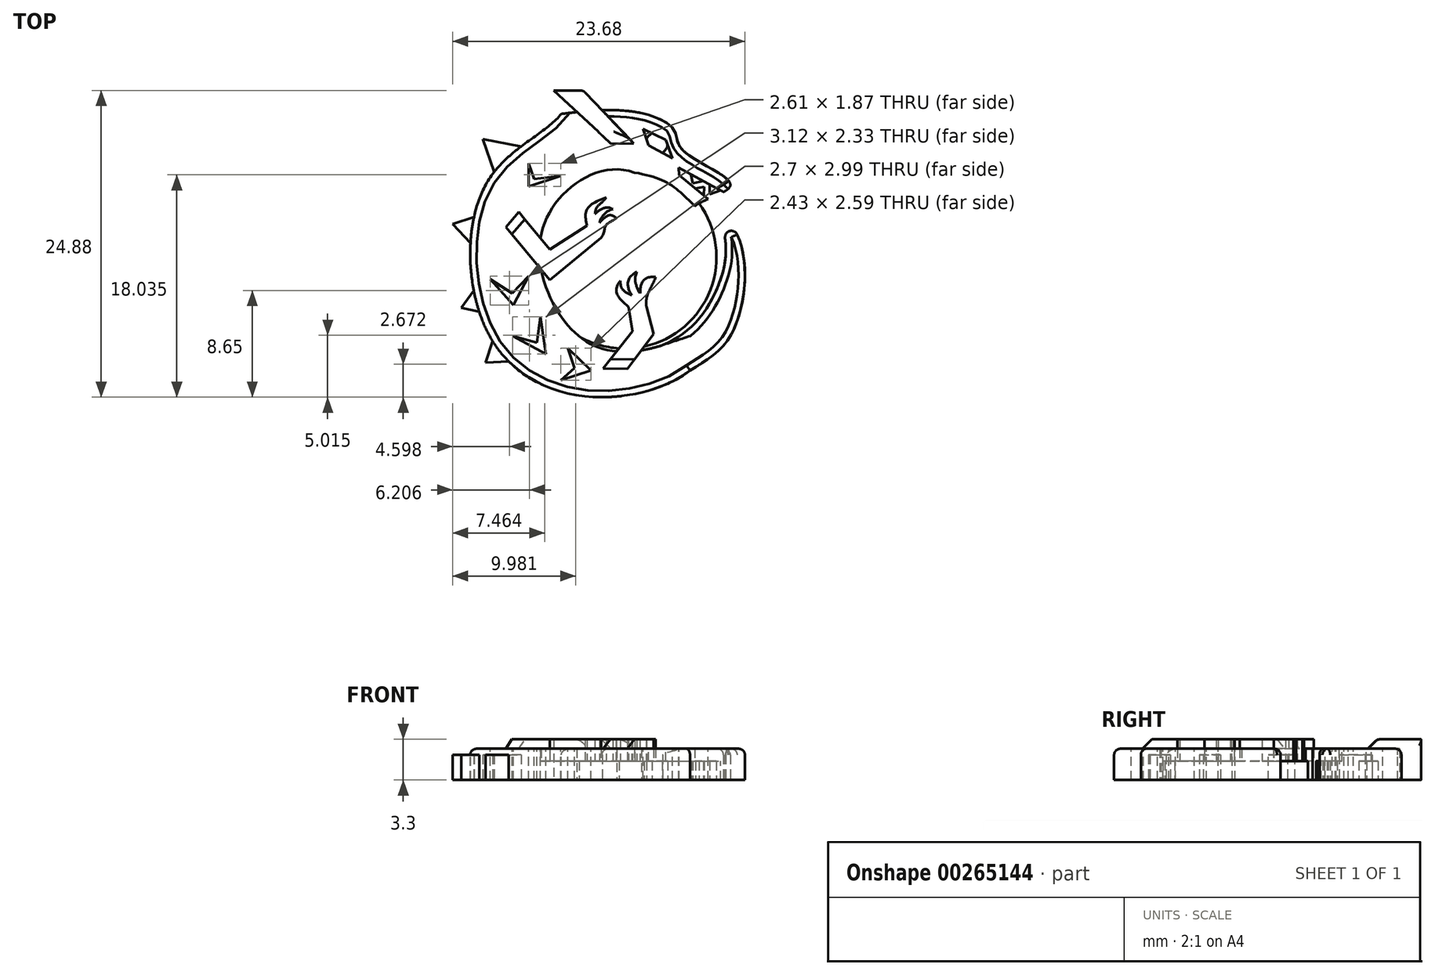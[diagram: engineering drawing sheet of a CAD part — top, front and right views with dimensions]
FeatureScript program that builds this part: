
annotation { "Feature Type Name" : "Feature", "Feature Type Description" : "" }
export const myFeature = defineFeature(function(context is Context, id is Id, definition is map)
    precondition{}
    {
        {
            var Q0;
            Q0=qCreatedBy(makeId("Top.planeOp"),FACE);
            var sketch = newSketch(context, id + "F0", { "sketchPlane" : qUnion([Q0])});
            skCircle(sketch, "E0", {"center": v(0, 0) * mm, "radius": 12.7 * mm, "construction": true});
            skCircle(sketch, "E1", {"center": v(0, 0) * mm, "radius": 7.43 * mm});
            skSolve(sketch);
        }
        {
            var Q0;
            Q0=makeQuery(id+"F0.imprint","IMPRINT",FACE,{"disambiguationData":[TD([[makeQuery(id+"F0.imprint","IMPRINT",EDGE,{"derivedFrom":sQuery(id+"F0.wireOp",EDGE,"E1")}),1.0]])]});
            var Q1;
            Q1=sQuery(id+"F0.wireOp",EDGE,"E1");
            extrude(context, id + "F1", {"entities" : qUnion([Q0]), "surfaceEntities" : qUnion([Q1]), "depth" : 1.52 * mm});
        }
        {
            var Q0;
            Q0=qCreatedBy(makeId("Top.planeOp"),FACE);
            var sketch = newSketch(context, id + "F2", { "sketchPlane" : qUnion([Q0])});
            skCircle(sketch, "E2", {"center": v(0, 0) * mm, "radius": 12.7 * mm, "construction": true});
            skFitSpline(sketch, "E3", {"points": [v(-5.15, 11.6) * mm, v(-11.13, 6.12) * mm, v(-10.71, -6.82) * mm, v(-2.1, -11.36) * mm, v(5.28, -9.2) * mm], "startDerivative": vector(-16.37, -21.23) * mm, "endDerivative": vector(20.97, 16.77) * mm});
            skFitSpline(sketch, "E4", {"points": [v(0.8, 6.85) * mm, v(-6.42, 2.98) * mm, v(-5.45, -4.38) * mm, v(-1.56, -7.5) * mm, v(3.08, -7.14) * mm], "startDerivative": vector(-30.12, 10.9) * mm, "endDerivative": vector(18.36, 6.12) * mm});
            skFitSpline(sketch, "E5", {"points": [v(3.08, -7.14) * mm, v(7.52, -2.43) * mm, v(7.7, 3.63) * mm], "startDerivative": vector(15.11, 6.36) * mm, "endDerivative": vector(-4.84, 17.51) * mm});
            skFitSpline(sketch, "E6", {"points": [v(5.28, -9.2) * mm, v(8.88, -5.74) * mm, v(9.73, -1.63) * mm, v(7.7, 3.63) * mm], "startDerivative": vector(21.68, 12.67) * mm, "endDerivative": vector(-13.83, 11.17) * mm});
            skFitSpline(sketch, "E7", {"points": [v(-5.15, 11.6) * mm, v(1.6, 11.6) * mm, v(3.97, 10.34) * mm, v(4.4, 9.04) * mm, v(6.87, 7.25) * mm, v(8.54, 5.76) * mm, v(5.68, 4.14) * mm], "startDerivative": vector(39.1, 4.84) * mm, "endDerivative": vector(-16.82, -11.68) * mm});
            skFitSpline(sketch, "E8", {"points": [v(0.8, 6.85) * mm, v(3.88, 5.76) * mm, v(5.68, 4.14) * mm], "startDerivative": vector(7.86, -1.41) * mm, "endDerivative": vector(3.87, -3.38) * mm});
            skSolve(sketch);
        }
        {
            var Q0;
            Q0 = qSketchRegion(id + "F2", true);
            extrude(context, id + "F3", {"entities" : qUnion([Q0]), "operationType" : NewBodyOperationType.ADD, "depth" : 2.54 * mm});
        }
        {
            var Q0;
            Q0=qCreatedBy(makeId("Top.planeOp"),FACE);
            var sketch = newSketch(context, id + "F4", { "sketchPlane" : qUnion([Q0])});
            skLineSegment(sketch, "E9", {"start": v(-1.93, 9.95) * mm, "end": v(-5.76, 13.5) * mm});
            skLineSegment(sketch, "E10", {"start": v(-5.76, 13.5) * mm, "end": v(-3.37, 13.5) * mm});
            skLineSegment(sketch, "E11", {"start": v(-3.37, 13.5) * mm, "end": v(0, 9.97) * mm});
            skLineSegment(sketch, "E12", {"start": v(0, 9.97) * mm, "end": v(-1.93, 9.95) * mm});
            skLineSegment(sketch, "E13", {"start": v(-8.1, 3.06) * mm, "end": v(-6.08, 0.61) * mm});
            skLineSegment(sketch, "E14", {"start": v(-6.08, 0.61) * mm, "end": v(-3.06, 2.54) * mm});
            skLineSegment(sketch, "E15", {"start": v(-8.1, 3.06) * mm, "end": v(-9.14, 1.84) * mm});
            skPoint(sketch, "E15.endSnap0", {"position": v(-7.09, 1.84) * mm});
            skLineSegment(sketch, "E16", {"start": v(-9.14, 1.84) * mm, "end": v(-6.08, -1.86) * mm});
            skLineSegment(sketch, "E17", {"start": v(-6.08, -1.86) * mm, "end": v(-1.93, 1.58) * mm});
            skLineSegment(sketch, "E18", {"start": v(-1.17, -8.27) * mm, "end": v(0.63, -6.04) * mm});
            skLineSegment(sketch, "E19", {"start": v(0.63, -6.04) * mm, "end": v(0.32, -4.04) * mm});
            skLineSegment(sketch, "E20", {"start": v(1.76, -4.04) * mm, "end": v(2.33, -6.23) * mm});
            skLineSegment(sketch, "E21", {"start": v(2.33, -6.23) * mm, "end": v(0.78, -8.3) * mm});
            skLineSegment(sketch, "E22", {"start": v(0.78, -8.3) * mm, "end": v(-1.17, -8.27) * mm});
            skFitSpline(sketch, "E23", {"points": [v(-3.06, 2.54) * mm, v(-3.06, 3.89) * mm, v(-1.5, 4.83) * mm], "startDerivative": vector(-0.67, 3.2) * mm, "endDerivative": vector(3.68, 1.43) * mm});
            skFitSpline(sketch, "E24", {"points": [v(-2.42, 3.49) * mm, v(-2.23, 4.07) * mm, v(-1.5, 4.83) * mm], "startDerivative": vector(0.18, 1.81) * mm, "endDerivative": vector(1.3, 1.74) * mm});
            skFitSpline(sketch, "E25", {"points": [v(0.32, -4.04) * mm, v(-0.6, -3.02) * mm, v(-0.36, -1.94) * mm], "startDerivative": vector(-2.36, 1.84) * mm, "endDerivative": vector(2.3, 2.4) * mm});
            skFitSpline(sketch, "E26", {"points": [v(-0.36, -1.94) * mm, v(-0.13, -2.69) * mm, v(0.57, -3.1) * mm], "startDerivative": vector(0.12, -2.92) * mm, "endDerivative": vector(1.41, -0.47) * mm});
            skFitSpline(sketch, "E27", {"points": [v(-2.42, 3.49) * mm, v(-1.69, 3.97) * mm, v(-0.97, 3.89) * mm], "startDerivative": vector(0.9, 1.26) * mm, "endDerivative": vector(1.9, -1) * mm});
            skFitSpline(sketch, "E28", {"points": [v(-2.05, 2.79) * mm, v(-1.69, 3.44) * mm, v(-0.97, 3.89) * mm], "startDerivative": vector(0.91, 2.74) * mm, "endDerivative": vector(3.06, 0.9) * mm});
            skFitSpline(sketch, "E29", {"points": [v(-2.05, 2.79) * mm, v(-1.33, 3.37) * mm, v(-0.68, 3.15) * mm], "startDerivative": vector(1.35, 1.5) * mm, "endDerivative": vector(1.95, -1.58) * mm});
            skFitSpline(sketch, "E30", {"points": [v(-1.93, 1.58) * mm, v(-1.57, 2.5) * mm, v(-0.68, 3.15) * mm], "startDerivative": vector(1.99, 1.83) * mm, "endDerivative": vector(2.18, 1.57) * mm});
            skFitSpline(sketch, "E31", {"points": [v(0.98, -1.2) * mm, v(0.88, -2.12) * mm, v(1.24, -2.94) * mm], "startDerivative": vector(-1.16, -2.8) * mm, "endDerivative": vector(1.21, -1.5) * mm});
            skFitSpline(sketch, "E32", {"points": [v(1.24, -2.94) * mm, v(1.4, -2.05) * mm, v(2.5, -1.62) * mm], "startDerivative": vector(0.1, 1.86) * mm, "endDerivative": vector(3.18, -0.4) * mm});
            skFitSpline(sketch, "E33", {"points": [v(1.76, -4.04) * mm, v(1.91, -2.89) * mm, v(2.5, -1.62) * mm], "startDerivative": vector(-0.52, 2.56) * mm, "endDerivative": vector(0.9, 2.41) * mm});
            skFitSpline(sketch, "E34", {"points": [v(0.57, -3.1) * mm, v(0.26, -2.36) * mm, v(0.98, -1.2) * mm], "startDerivative": vector(-0.97, 1.51) * mm, "endDerivative": vector(3.47, 1.65) * mm});
            skSolve(sketch);
        }
        {
            var Q0;
            Q0 = qSketchRegion(id + "F4", true);
            extrude(context, id + "F5", {"entities" : qUnion([Q0]), "operationType" : NewBodyOperationType.ADD, "depth" : 3.3 * mm});
        }
        {
            var Q0;
            Q0=makeQuery(id+"F3.opExtrude","CAP_FACE",FACE,{"disambiguationData":[OSD([sQuery(id+"F2.wireOp",EDGE,"E3"),sQuery(id+"F2.wireOp",EDGE,"E4"),sQuery(id+"F2.wireOp",EDGE,"E5"),sQuery(id+"F2.wireOp",EDGE,"E6"),sQuery(id+"F2.wireOp",EDGE,"E7"),sQuery(id+"F2.wireOp",EDGE,"E8")])],"isStart":false});
            var sketch = newSketch(context, id + "F6", { "sketchPlane" : qUnion([Q0])});
            skLineSegment(sketch, "E35", {"start": v(1.46, 10.4) * mm, "end": v(3.32, 9.5) * mm});
            skLineSegment(sketch, "E36", {"start": v(3.32, 9.5) * mm, "end": v(3.86, 8.02) * mm});
            skLineSegment(sketch, "E37", {"start": v(3.86, 8.02) * mm, "end": v(1.93, 9.07) * mm});
            skLineSegment(sketch, "E38", {"start": v(1.93, 9.07) * mm, "end": v(1.46, 10.4) * mm});
            skLineSegment(sketch, "E39", {"start": v(4.4, 6.64) * mm, "end": v(6.75, 4.7) * mm});
            skLineSegment(sketch, "E40", {"start": v(6.75, 4.7) * mm, "end": v(8.23, 5.16) * mm});
            skLineSegment(sketch, "E41", {"start": v(8.23, 5.16) * mm, "end": v(4.36, 7.26) * mm});
            skLineSegment(sketch, "E42", {"start": v(4.36, 7.26) * mm, "end": v(4.4, 6.64) * mm});
            skSolve(sketch);
        }
        {
            var Q0;
            Q0 = qSketchRegion(id + "F6", true);
            extrude(context, id + "F7", {"entities" : qUnion([Q0]), "operationType" : NewBodyOperationType.REMOVE, "oppositeDirection" : true, "depth" : 25.4 * mm});
        }
        {
            var Q0;
            Q0=makeQuery(id+"F5.boolean.opBoolean","INTERSECT",EDGE,{"derivedFrom":[makeQuery(id+"F3.opExtrude","CAP_FACE",FACE,{"disambiguationData":[OSD([sQuery(id+"F2.wireOp",EDGE,"E3"),sQuery(id+"F2.wireOp",EDGE,"E4"),sQuery(id+"F2.wireOp",EDGE,"E5"),sQuery(id+"F2.wireOp",EDGE,"E6"),sQuery(id+"F2.wireOp",EDGE,"E7"),sQuery(id+"F2.wireOp",EDGE,"E8")])],"isStart":false}),makeQuery(id+"F5.opExtrude","SWEPT_FACE",FACE,{"disambiguationData":[OSD([sQuery(id+"F4.wireOp",EDGE,"E15")])]})]});
            var Q1;
            Q1=makeQuery(id+"F5.boolean.opBoolean","INTERSECT",EDGE,{"derivedFrom":[makeQuery(id+"F3.opExtrude","CAP_FACE",FACE,{"disambiguationData":[OSD([sQuery(id+"F2.wireOp",EDGE,"E3"),sQuery(id+"F2.wireOp",EDGE,"E4"),sQuery(id+"F2.wireOp",EDGE,"E5"),sQuery(id+"F2.wireOp",EDGE,"E6"),sQuery(id+"F2.wireOp",EDGE,"E7"),sQuery(id+"F2.wireOp",EDGE,"E8")])],"isStart":false}),makeQuery(id+"F5.opExtrude","SWEPT_FACE",FACE,{"disambiguationData":[OSD([sQuery(id+"F4.wireOp",EDGE,"E12")])]})]});
            var Q2;
            Q2=makeQuery(id+"F5.boolean.opBoolean","INTERSECT",EDGE,{"derivedFrom":[makeQuery(id+"F3.opExtrude","CAP_FACE",FACE,{"disambiguationData":[OSD([sQuery(id+"F2.wireOp",EDGE,"E3"),sQuery(id+"F2.wireOp",EDGE,"E4"),sQuery(id+"F2.wireOp",EDGE,"E5"),sQuery(id+"F2.wireOp",EDGE,"E6"),sQuery(id+"F2.wireOp",EDGE,"E7"),sQuery(id+"F2.wireOp",EDGE,"E8")])],"isStart":false}),makeQuery(id+"F5.opExtrude","SWEPT_FACE",FACE,{"disambiguationData":[OSD([sQuery(id+"F4.wireOp",EDGE,"E22")])]})]});
            chamfer(context, id + "F8", {"entities" : qUnion([Q0, Q1, Q2]), "width" : 0.76 * mm, "tangentPropagation" : true});
        }
        {
            var Q0;
            Q0=makeQuery(id+"F3.opExtrude","CAP_EDGE",EDGE,{"disambiguationData":[OSD([sQuery(id+"F2.wireOp",EDGE,"E3")])],"isStart":false});
            var Q1;
            Q1=makeQuery(id+"F3.opExtrude","CAP_EDGE",EDGE,{"disambiguationData":[OSD([sQuery(id+"F2.wireOp",EDGE,"E6")])],"isStart":false});
            fillet(context, id + "F9", {"entities" : qUnion([Q0, Q1]), "radius" : 0.5 * mm, "allowEdgeOverflow" : false});
        }
        {
            var Q0;
            Q0=qCreatedBy(makeId("Top.planeOp"),FACE);
            var sketch = newSketch(context, id + "F10", { "sketchPlane" : qUnion([Q0])});
            skCircle(sketch, "E43", {"center": v(2.59, 9.23) * mm, "radius": 0.89 * mm});
            skLineSegment(sketch, "E44", {"start": v(5.36, 6.71) * mm, "end": v(5.51, 5.98) * mm});
            skLineSegment(sketch, "E45", {"start": v(5.51, 5.98) * mm, "end": v(6.37, 6.16) * mm});
            skLineSegment(sketch, "E46", {"start": v(6.37, 6.16) * mm, "end": v(6.87, 5.9) * mm});
            skLineSegment(sketch, "E47", {"start": v(6.87, 5.9) * mm, "end": v(6.87, 5.1) * mm});
            skLineSegment(sketch, "E48", {"start": v(6.87, 5.1) * mm, "end": v(7.8, 5.42) * mm});
            skLineSegment(sketch, "E49", {"start": v(7.8, 5.42) * mm, "end": v(7.18, 6.6) * mm});
            skLineSegment(sketch, "E50", {"start": v(7.18, 6.6) * mm, "end": v(5.36, 6.71) * mm});
            skLineSegment(sketch, "E51", {"start": v(5.72, 5.55) * mm, "end": v(6.43, 5.68) * mm});
            skLineSegment(sketch, "E52", {"start": v(6.43, 5.68) * mm, "end": v(6.39, 5) * mm});
            skLineSegment(sketch, "E53", {"start": v(6.39, 5) * mm, "end": v(5.72, 5.55) * mm});
            skSolve(sketch);
        }
        {
            var Q0;
            Q0 = qSketchRegion(id + "F10", true);
            extrude(context, id + "F11", {"entities" : qUnion([Q0]), "operationType" : NewBodyOperationType.ADD, "depth" : 1.52 * mm});
        }
        {
            var Q0;
            Q0=makeQuery(id+"F3.opExtrude","CAP_FACE",FACE,{"disambiguationData":[OSD([sQuery(id+"F2.wireOp",EDGE,"E3"),sQuery(id+"F2.wireOp",EDGE,"E4"),sQuery(id+"F2.wireOp",EDGE,"E5"),sQuery(id+"F2.wireOp",EDGE,"E6"),sQuery(id+"F2.wireOp",EDGE,"E7"),sQuery(id+"F2.wireOp",EDGE,"E8")])],"isStart":false});
            var sketch = newSketch(context, id + "F12", { "sketchPlane" : qUnion([Q0])});
            skLineSegment(sketch, "E54", {"start": v(-7.8, 7.6) * mm, "end": v(-7.8, 5.73) * mm});
            skLineSegment(sketch, "E55", {"start": v(-7.8, 5.73) * mm, "end": v(-5.18, 6.57) * mm});
            skLineSegment(sketch, "E56", {"start": v(-5.18, 6.57) * mm, "end": v(-7.34, 6.32) * mm});
            skLineSegment(sketch, "E57", {"start": v(-7.34, 6.32) * mm, "end": v(-7.8, 7.6) * mm});
            skLineSegment(sketch, "E58", {"start": v(-10.91, -1.8) * mm, "end": v(-9.04, -3.88) * mm});
            skLineSegment(sketch, "E59", {"start": v(-9.04, -3.88) * mm, "end": v(-7.8, -1.56) * mm});
            skLineSegment(sketch, "E60", {"start": v(-7.8, -1.56) * mm, "end": v(-9.11, -2.93) * mm});
            skLineSegment(sketch, "E61", {"start": v(-9.11, -2.93) * mm, "end": v(-10.91, -1.8) * mm});
            skLineSegment(sketch, "E62", {"start": v(-9.1, -6.4) * mm, "end": v(-6.4, -7.85) * mm});
            skLineSegment(sketch, "E63", {"start": v(-6.4, -7.85) * mm, "end": v(-6.84, -4.86) * mm});
            skLineSegment(sketch, "E64", {"start": v(-6.84, -4.86) * mm, "end": v(-7.1, -6.93) * mm});
            skLineSegment(sketch, "E65", {"start": v(-7.1, -6.93) * mm, "end": v(-9.1, -6.4) * mm});
            skLineSegment(sketch, "E66", {"start": v(-4.6, -7.4) * mm, "end": v(-4.09, -9) * mm});
            skLineSegment(sketch, "E67", {"start": v(-4.09, -9) * mm, "end": v(-5.18, -10) * mm});
            skLineSegment(sketch, "E68", {"start": v(-5.18, -10) * mm, "end": v(-2.76, -9.2) * mm});
            skLineSegment(sketch, "E69", {"start": v(-2.76, -9.2) * mm, "end": v(-4.6, -7.4) * mm});
            skSolve(sketch);
        }
        {
            var Q0;
            Q0 = qSketchRegion(id + "F12", true);
            extrude(context, id + "F13", {"entities" : qUnion([Q0]), "operationType" : NewBodyOperationType.REMOVE, "oppositeDirection" : true, "depth" : 25.4 * mm});
        }
        {
            var Q0;
            {var subQ0=sQuery(id+"F2.wireOp",EDGE,"E8");var subQ1=sQuery(id+"F2.wireOp",EDGE,"E7");var subQ4=makeQuery(id+"F5.opExtrude","SWEPT_FACE",FACE,{"disambiguationData":[OSD([sQuery(id+"F4.wireOp",EDGE,"E11")])]});Q0=makeQuery(id+"F7.boolean.opBoolean","SPLIT",EDGE,{"disambiguationData":[TD([subQ4])],"derivedFrom":makeQuery(id+"F5.boolean.opBoolean","SPLIT",EDGE,{"disambiguationData":[TD([makeQuery(id+"F3.opExtrude","SWEPT_FACE",FACE,{"disambiguationData":[OSD([subQ0])]})])],"derivedFrom":makeQuery(id+"F3.opExtrude","CAP_EDGE",EDGE,{"disambiguationData":[OSD([subQ1])],"isStart":false})})});}
            var Q1;
            Q1=makeQuery(id+"F3.opExtrude","CAP_EDGE",EDGE,{"disambiguationData":[OSD([sQuery(id+"F2.wireOp",EDGE,"E5")])],"isStart":false});
            var Q2;
            Q2=makeQuery(id+"F5.opExtrude","SWEPT_EDGE",EDGE,{"disambiguationData":[OSD([sQuery(id+"F4.wireOp",EDGE,"E10"),sQuery(id+"F4.wireOp",EDGE,"E11")])]});
            var Q3;
            Q3=makeQuery(id+"F5.opExtrude","CAP_EDGE",EDGE,{"disambiguationData":[OSD([sQuery(id+"F4.wireOp",EDGE,"E11")])],"isStart":false});
            var Q4;
            {var subQ0=sQuery(id+"F4.wireOp",EDGE,"E12");Q4=makeQuery(id+"F8.opChamfer","BLEND_EDGE",EDGE,{"blendedFrom":[makeQuery(id+"F5.boolean.opBoolean","INTERSECT",EDGE,{"derivedFrom":[makeQuery(id+"F3.opExtrude","CAP_FACE",FACE,{"disambiguationData":[OSD([sQuery(id+"F2.wireOp",EDGE,"E3"),sQuery(id+"F2.wireOp",EDGE,"E4"),sQuery(id+"F2.wireOp",EDGE,"E5"),sQuery(id+"F2.wireOp",EDGE,"E6"),sQuery(id+"F2.wireOp",EDGE,"E7"),sQuery(id+"F2.wireOp",EDGE,"E8")])],"isStart":false}),makeQuery(id+"F5.opExtrude","SWEPT_FACE",FACE,{"disambiguationData":[OSD([subQ0])]})]}),makeQuery(id+"F5.opExtrude","CAP_FACE",FACE,{"disambiguationData":[OSD([sQuery(id+"F4.wireOp",EDGE,"E9"),sQuery(id+"F4.wireOp",EDGE,"E10"),sQuery(id+"F4.wireOp",EDGE,"E11"),subQ0])],"isStart":false})],"blendedInto":[makeQuery(id+"F5.opExtrude","CAP_FACE",FACE,{"disambiguationData":[OSD([sQuery(id+"F4.wireOp",EDGE,"E9"),sQuery(id+"F4.wireOp",EDGE,"E10"),sQuery(id+"F4.wireOp",EDGE,"E11"),subQ0])],"isStart":false})]});}
            fillet(context, id + "F14", {"entities" : qUnion([Q0, Q1, Q2, Q3, Q4]), "radius" : 0.5 * mm, "tangentPropagation" : true, "allowEdgeOverflow" : false});
        }
        {
            var Q0;
            Q0=qCreatedBy(makeId("Top.planeOp"),FACE);
            var sketch = newSketch(context, id + "F15", { "sketchPlane" : qUnion([Q0])});
            skLineSegment(sketch, "E70", {"start": v(-7.13, 8.72) * mm, "end": v(-11.5, 9.55) * mm});
            skLineSegment(sketch, "E71", {"start": v(-11.5, 9.55) * mm, "end": v(-9.94, 4.93) * mm});
            skLineSegment(sketch, "E72", {"start": v(-9.94, 4.93) * mm, "end": v(-7.13, 8.72) * mm});
            skLineSegment(sketch, "E73", {"start": v(-10.28, 3.91) * mm, "end": v(-13.95, 2.67) * mm});
            skLineSegment(sketch, "E74", {"start": v(-13.95, 2.67) * mm, "end": v(-10.93, -0.58) * mm});
            skLineSegment(sketch, "E75", {"start": v(-10.93, -0.58) * mm, "end": v(-10.28, 3.91) * mm});
            skLineSegment(sketch, "E76", {"start": v(-10.34, -5.6) * mm, "end": v(-11.3, -8.58) * mm});
            skLineSegment(sketch, "E77", {"start": v(-11.3, -8.58) * mm, "end": v(-7.43, -8.33) * mm});
            skLineSegment(sketch, "E78", {"start": v(-7.43, -8.33) * mm, "end": v(-10.34, -5.6) * mm});
            skLineSegment(sketch, "E79", {"start": v(-11.45, -1.62) * mm, "end": v(-13.24, -4.13) * mm});
            skLineSegment(sketch, "E80", {"start": v(-13.24, -4.13) * mm, "end": v(-10.46, -4.74) * mm});
            skLineSegment(sketch, "E81", {"start": v(-10.46, -4.74) * mm, "end": v(-11.45, -1.62) * mm});
            skSolve(sketch);
        }
        {
            var Q0;
            Q0 = qSketchRegion(id + "F15", true);
            extrude(context, id + "F16", {"entities" : qUnion([Q0]), "operationType" : NewBodyOperationType.ADD, "depth" : 2.03 * mm});
        }
    });
